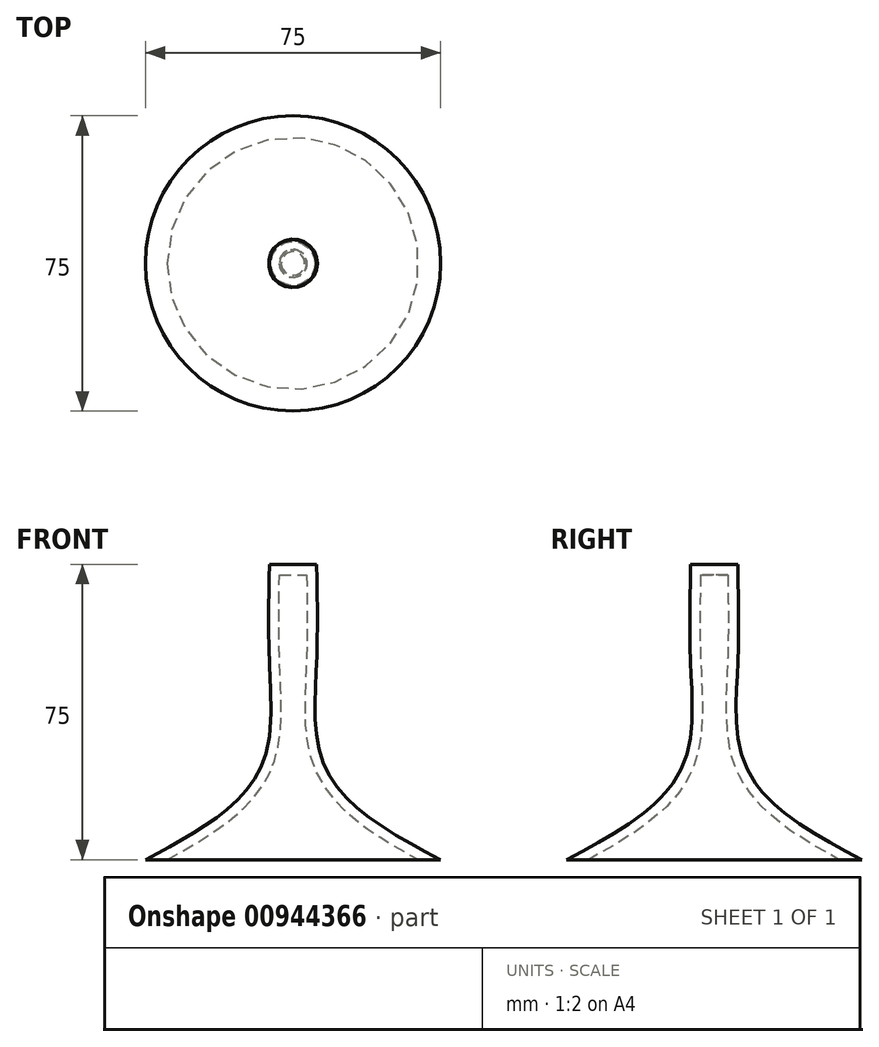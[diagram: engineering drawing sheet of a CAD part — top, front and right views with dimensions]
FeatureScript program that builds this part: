
annotation { "Feature Type Name" : "Feature", "Feature Type Description" : "" }
export const myFeature = defineFeature(function(context is Context, id is Id, definition is map)
    precondition{}
    {
        {
            var Q0;
            Q0=qCreatedBy(makeId("Top.planeOp"),FACE);
            var sketch = newSketch(context, id + "F0", { "sketchPlane" : qUnion([Q0])});
            skCircle(sketch, "E0", {"center": v(0, 0) * mm, "radius": 6 * mm});
            skSolve(sketch);
        }
        {
            var Q0;
            Q0=qCreatedBy(makeId("Top.planeOp"),FACE);
            cPlane(context, id + "F1", {"entities" : qUnion([Q0]), "cplaneType" : CPlaneType.OFFSET, "offset" : 50 * mm, "oppositeDirection" : true, "width" : 150 * mm, "height" : 150 * mm});
        }
        {
            var Q0;
            Q0=qCreatedBy(id+"F1.planeOp",FACE);
            var sketch = newSketch(context, id + "F2", { "sketchPlane" : qUnion([Q0])});
            skCircle(sketch, "E1", {"center": v(0, 0) * mm, "radius": 37.5 * mm});
            skSolve(sketch);
        }
        {
            var Q0;
            Q0=qCreatedBy(makeId("Top.planeOp"),FACE);
            cPlane(context, id + "F3", {"entities" : qUnion([Q0]), "cplaneType" : CPlaneType.OFFSET, "offset" : 25 * mm, "oppositeDirection" : true, "width" : 150 * mm, "height" : 150 * mm});
        }
        {
            var Q0;
            Q0=qCreatedBy(makeId("Top.planeOp"),FACE);
            cPlane(context, id + "F4", {"entities" : qUnion([Q0]), "cplaneType" : CPlaneType.OFFSET, "offset" : 25 * mm, "width" : 150 * mm, "height" : 150 * mm});
        }
        {
            var Q0;
            Q0=qCreatedBy(id+"F3.planeOp",FACE);
            var sketch = newSketch(context, id + "F5", { "sketchPlane" : qUnion([Q0])});
            skCircle(sketch, "E2", {"center": v(0, 0) * mm, "radius": 7.5 * mm});
            skSolve(sketch);
        }
        {
            var Q0;
            Q0=qCreatedBy(id+"F4.planeOp",FACE);
            var sketch = newSketch(context, id + "F6", { "sketchPlane" : qUnion([Q0])});
            skCircle(sketch, "E3", {"center": v(0, 0) * mm, "radius": 6 * mm});
            skSolve(sketch);
        }
        {
            var Q0;
            Q0=makeQuery(id+"F2.imprint","IMPRINT",FACE,{"disambiguationData":[TD([[makeQuery(id+"F2.imprint","IMPRINT",EDGE,{"derivedFrom":sQuery(id+"F2.wireOp",EDGE,"E1")}),1.0]])]});
            var Q1;
            Q1=makeQuery(id+"F5.imprint","IMPRINT",FACE,{"disambiguationData":[TD([[makeQuery(id+"F5.imprint","IMPRINT",EDGE,{"derivedFrom":sQuery(id+"F5.wireOp",EDGE,"E2")}),1.0]])]});
            var Q2;
            Q2=makeQuery(id+"F0.imprint","IMPRINT",FACE,{"disambiguationData":[TD([[makeQuery(id+"F0.imprint","IMPRINT",EDGE,{"derivedFrom":sQuery(id+"F0.wireOp",EDGE,"E0")}),1.0]])]});
            var Q3;
            Q3=makeQuery(id+"F6.imprint","IMPRINT",FACE,{"disambiguationData":[TD([[makeQuery(id+"F6.imprint","IMPRINT",EDGE,{"derivedFrom":sQuery(id+"F6.wireOp",EDGE,"E3")}),1.0]])]});
            loft(context, id + "F7", {"sheetProfilesArray" : [{ "sheetProfileEntities" : qUnion([Q0]) }, { "sheetProfileEntities" : qUnion([Q1]) }, { "sheetProfileEntities" : qUnion([Q2]) }, { "sheetProfileEntities" : qUnion([Q3]) }]});
        }
        {
            var Q0;
            Q0=makeQuery(id+"F7.opLoft","CAP_FACE",FACE,{"disambiguationData":[OSD([makeQuery(id+"F2.imprint","IMPRINT",FACE,{"disambiguationData":[TD([[makeQuery(id+"F2.imprint","IMPRINT",EDGE,{"derivedFrom":sQuery(id+"F2.wireOp",EDGE,"E1")}),1.0]])]})])],"isStart":true});
            shell(context, id + "F8", {"entities" : qUnion([Q0]), "thickness" : 2.6 * mm});
        }
    });
